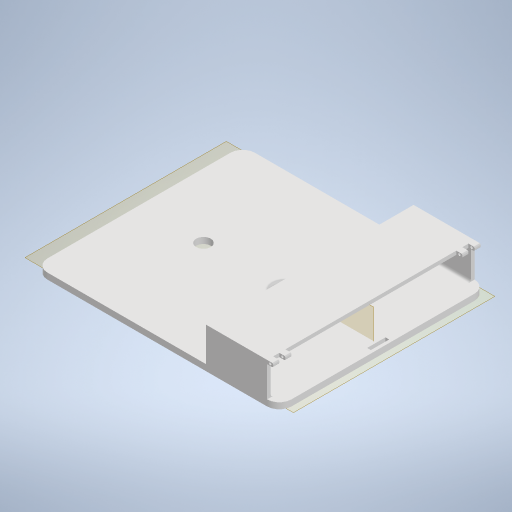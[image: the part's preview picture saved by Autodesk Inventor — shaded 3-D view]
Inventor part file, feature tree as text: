
AUTODESK INVENTOR PART (.ipt)
format: ipt  version: 2024 (Build 280153000, 153)  size: 485,888 bytes
history: native  units: mm
features: extrude x9, sketch x9, fillet x5, projected_geometry x4, reference x3, other x3, plane x2, mirror x2
ambient origin geometry x8: Origin, YZ Plane, XZ Plane, XY Plane, X Axis, Y Axis, Z Axis, Center Point
bodies: Solid1 (feature_tree)
feature tree (37):
  plane  "Work Plane1"
  extrude  "Extrusion1"  Depth=2.5mm
  extrude  "Extrusion2"  Depth=30.0mm
  fillet  "Fillet1"  Radius=20.0mm
  fillet  "Fillet2"  Radius=30.0mm
  extrude  "Extrusion3"  Depth=10.0mm
  extrude  "Extrusion4"  Depth=3.0mm
  fillet  "Fillet4"  Radius=3.0mm
  extrude  "Extrusion5"  Depth=10.0mm
  fillet  "Fillet5"  Radius=10.0mm
  extrude  "Extrusion6"  Depth=25.0mm TaperAngle=0.0deg
  plane  "Work Plane2"
  fillet  "Fillet6"  Radius=2.0mm
  extrude  "Extrusion7"  Depth=2.0mm
  mirror  "Mirror1"
  mirror  "Mirror2"
  extrude  "Extrusion8"  Depth=5.0mm
  extrude  "Extrusion9"  Depth=3.0mm
  sketch  "Sketch1"  dims[d0=2.5mm d1=2.5mm]
  reference  "Reference1"
  reference  "Reference2"
  reference  "Reference3"
  sketch  "Sketch2"  dims[d2=5.0mm d3=0.0mm d4=20.0mm d5=20.0mm d6=30.0mm]
  sketch  "Sketch5"  dims[d7=5.0mm d8=0.0mm d9=10.0mm]
  projected_geometry  "Projected Loop1"
  sketch  "Sketch6"  dims[d10=2.0mm d14=50.0mm d15=3.0mm]
  projected_geometry  "Projected Loop2"
  sketch  "Sketch8"  dims[d16=25.0mm d17=0.0mm d18=20.0mm d19=10.0mm]
  projected_geometry  "Projected Loop3"
  sketch  "Sketch9"  dims[d20=10.0mm d21=25.0mm d22=0.0mm d23=2.0mm]
  projected_geometry  "Projected Loop4"
  sketch  "Sketch10"  dims[d24=3.0mm d25=0.0mm d26=2.0mm]
  sketch  "Sketch11"  dims[d27=3.0mm d28=5.0mm]
  sketch  "Sketch12"  dims[d29=5.0mm d30=3.0mm d31=5.0mm d32=5.0mm d33=0.0mm d34=82.0mm d35=1.0mm d36=2.0mm d37=2.5mm d38=1.5mm d39=0.0mm d40=0.0mm d41=3.0mm d42=15.0mm d43=106.0mm d44=10.0mm d45=0.0mm d46=12.0mm d47=10.0mm d48=0.0mm]
  other  "<userpath> windows\Documents\Inventor\Robotska_roka\Assembly4.iam"
  other  "Assembly4.iam"
  other  "vozicek1:1"
